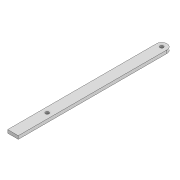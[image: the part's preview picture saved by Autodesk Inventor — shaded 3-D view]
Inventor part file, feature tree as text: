
AUTODESK INVENTOR PART (.ipt)
format: ipt  version: 2022 (Build 260153000, 153)  size: 98,304 bytes
history: native  units: mm
features: extrude x2, sketch x2
ambient origin geometry x8: Origin, YZ Plane, XZ Plane, XY Plane, X Axis, Y Axis, Z Axis, Center Point
bodies: Solid1 (feature_tree)
feature tree (4):
  extrude  "Extrusion1"  Depth=3.3mm
  extrude  "Extrusion2"  Depth=261.6mm
  sketch  "Sketch1"  dims[d0=3.3mm d1=3.3mm]
  sketch  "Sketch3"  dims[d2=10.0mm d3=261.6mm d4=3.3mm d5=153.559mm d6=3.0mm d7=0.0mm d8=100.0mm d9=0.0mm]
